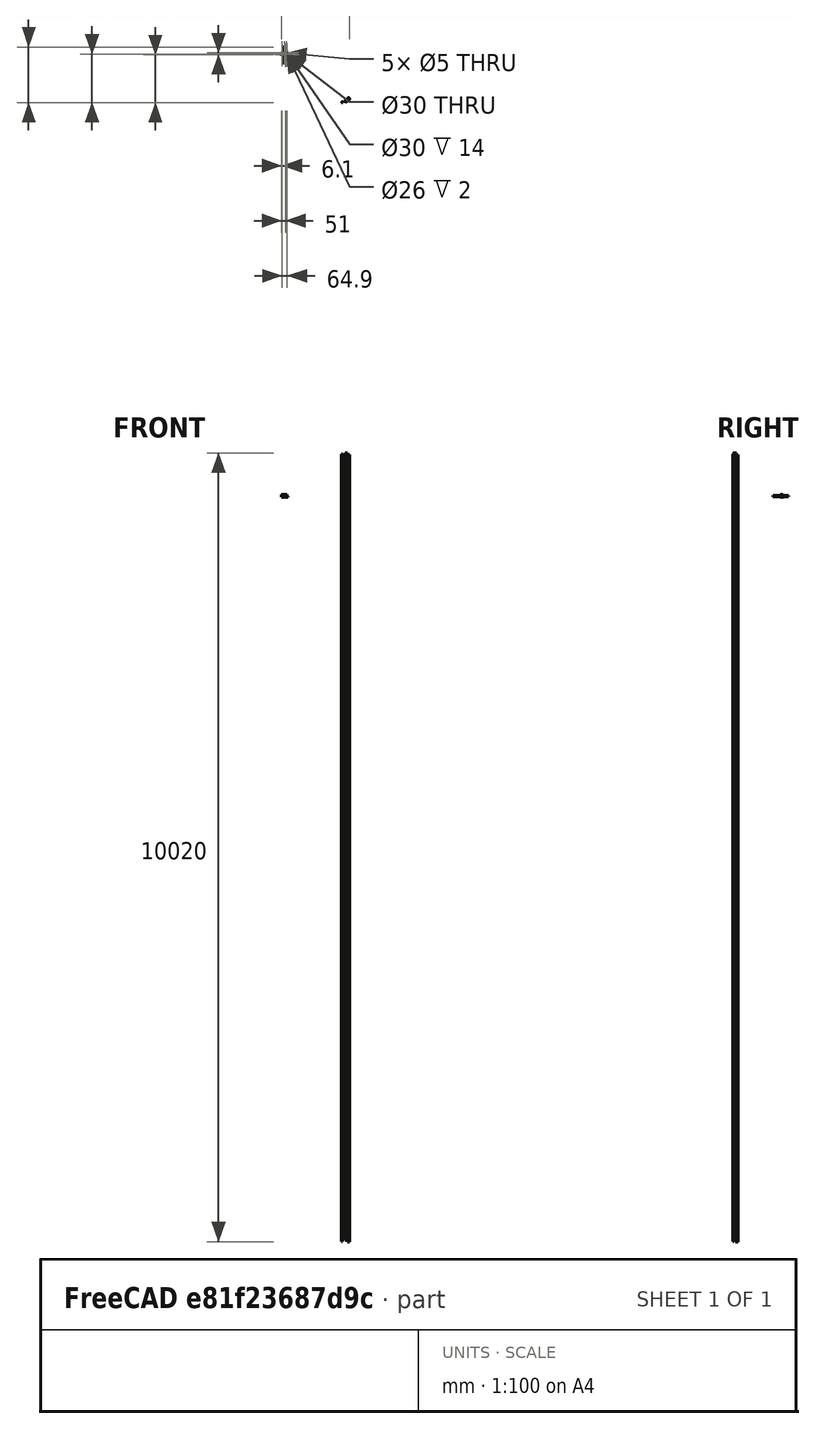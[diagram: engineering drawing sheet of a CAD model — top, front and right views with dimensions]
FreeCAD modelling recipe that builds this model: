
FCSTD DOCUMENT  (FreeCAD 0.15R4671 (Git))
Label: slide_rail_flange_mount_inset
License: CC-BY 3.0
LicenseURL: http://creativecommons.org/licenses/by/3.0/
objects: Sketcher::SketchObject×7, PartDesign::Pocket×6, Part::Cylinder×3, Part::Box×3, Mesh::Feature×2, PartDesign::Fillet×2, PartDesign::Pad×1, Part::Feature×1, Part::MultiFuse×1, Part::Cut×1
note: 32 computed .brp shape members not serialized (recipe doc carries the construction recipe); baked Part::Feature solids carry a one-line shape summary decoded from their .brp

FEATURE [Mesh::Feature] tmp  label="plate"
FEATURE [Part::Cylinder] Cylinder  label="bearing"
  Angle = 360
  Height = 9
  Placement = pos=(-717,613,-534) rot=(0,0,1;0rad)
  Radius = 15
FEATURE [Mesh::Feature] lead_screw_flange  label="lead-screw-flange"
  Placement = pos=(-747,556,-523) rot=(0,0.707107,0.707107;3.14159rad)
FEATURE [Part::Cylinder] Cylinder001  label="lead_screw"
  Angle = 360
  Height = 200
  Placement = pos=(-747,700,-523) rot=(1,0,0;1.5708rad)
  Radius = 5.556
FEATURE [Sketcher::SketchObject] Sketch
  Placement = pos=(-717,613,-525) rot=(0,0,1;0rad)
  Support = -> Cylinder [Face2]
  sketch-geometry (1):
    g0: Circle CenterX=0 CenterY=0 CenterZ=0 NormalX=0 NormalY=0 NormalZ=1 Radius=5
  constraints (2):
    c: Radius(g0) = 5
    c: Coincident(g0,g-1)
FEATURE [PartDesign::Pocket] Pocket
  Length = 5
  Placement = pos=(-717,613,-534) rot=(0,0,1;0rad)
  Sketch = -> Sketch
  Type = 1
FEATURE [Part::Box] Box  label="Cube"
  Height = 4
  Length = 80
  Placement = pos=(-768,594,-534) rot=(0,0,1;0rad)
  Width = 42
FEATURE [Sketcher::SketchObject] Sketch001
  Placement = pos=(-768,594,-530) rot=(0,0,1;0rad)
  Support = -> Box [Face6]
  sketch-geometry (1):
    g0: Circle CenterX=82 CenterY=41 CenterZ=0 NormalX=0 NormalY=0 NormalZ=1 Radius=15
  constraints (3):
    c: DistanceX(g-1,g0) = 82
    c: DistanceY(g-1,g0) = 41
    c: Radius(g0) = 15
FEATURE [PartDesign::Pocket] Pocket001
  Length = 5
  Placement = pos=(-768,594,-534) rot=(0,0,1;0rad)
  Sketch = -> Sketch001
  Type = 1
FEATURE [Part::Box] Box001  label="Cube001"
  Height = 25
  Length = 40
  Placement = pos=(-768,594,-530) rot=(0,0,1;0rad)
  Width = 4
FEATURE [Sketcher::SketchObject] Sketch002
  Placement = pos=(-768,598,-530) rot=(0,0.707107,0.707107;3.14159rad)
  Support = -> Box001 [Face4]
  sketch-geometry (6):
    g0: Circle CenterX=-33.247 CenterY=14 CenterZ=0 NormalX=0 NormalY=0 NormalZ=1 Radius=2.5781
    g1: Circle CenterX=-8.5 CenterY=14 CenterZ=0 NormalX=0 NormalY=0 NormalZ=1 Radius=2.5781
    g2: ArcOfCircle CenterX=-20.85 CenterY=12 CenterZ=0 NormalX=0 NormalY=0 NormalZ=1 Radius=7.15 StartAngle=0 EndAngle=3.14159
    g3: LineSegment StartX=-13.7 StartY=12 StartZ=0 EndX=-13.7 EndY=0 EndZ=0
    g4: LineSegment StartX=-28 StartY=12 StartZ=0 EndX=-28 EndY=0 EndZ=0
    g5: LineSegment StartX=-28 StartY=0 StartZ=0 EndX=-13.7 EndY=0 EndZ=0
  constraints (21):
    c: Radius(g0) = 2.5781
    c: Equal(g0,g1)
    c: DistanceY(g-1,g0) = 14
    c: DistanceY(g-1,g1) = 14
    c: DistanceX(g0,g1) = 24.747
    c: DistanceX(g-1,g1) = -8.5
    c: DistanceY(g-1,g2) = 12
    c: DistanceX(g-1,g2) = -20.85
    c: DistanceY(g-1,g2) = 12
    c: DistanceY(g-1,g2) = 12
    c: DistanceX(g-1,g2) = -28
    c: PointOnObject(g3,g-1)
    c: Vertical(g3)
    c: Tangent(g3,g2)
    c: PointOnObject(g4,g-1)
    c: Vertical(g4)
    c: Tangent(g4,g2)
    c: Coincident(g2,g4)
    c: Coincident(g3,g2)
    c: Coincident(g5,g4)
    c: Coincident(g5,g3)
FEATURE [PartDesign::Pocket] Pocket002
  Length = 5
  Placement = pos=(-768,594,-530) rot=(0,0,1;0rad)
  Sketch = -> Sketch002
  Type = 1
FEATURE [PartDesign::Fillet] Fillet
  Base = -> Pocket002 [Edge15]
  Placement = pos=(-768,594,-530) rot=(0,0,1;0rad)
  Radius = 10
FEATURE [PartDesign::Fillet] Fillet001
  Base = -> Fillet [Edge20]
  Placement = pos=(-768,594,-530) rot=(0,0,1;0rad)
  Radius = 10
FEATURE [Sketcher::SketchObject] Sketch003
  Placement = pos=(-768,594,-530) rot=(0,0,1;0rad)
  Support = -> Pocket001 [Face3]
  sketch-geometry (1):
    g0: Circle CenterX=51 CenterY=19 CenterZ=0 NormalX=0 NormalY=0 NormalZ=1 Radius=17
  constraints (3):
    c: Radius(g0) = 17
    c: DistanceY(g-1,g0) = 19
    c: DistanceX(g-1,g0) = 51
FEATURE [PartDesign::Pad] Pad
  Length = 20
  Length2 = 100
  Placement = pos=(-768,594,-534) rot=(0,0,1;0rad)
  Sketch = -> Sketch003
  Type = 0
FEATURE [Sketcher::SketchObject] Sketch004
  Placement = pos=(-768,594,-510) rot=(0,0,1;0rad)
  Support = -> Pad [Face9]
  sketch-geometry (1):
    g0: Circle CenterX=51 CenterY=19 CenterZ=0 NormalX=0 NormalY=0 NormalZ=1 Radius=15
  constraints (3):
    c: Radius(g0) = 15
    c: DistanceX(g-1,g0) = 51
    c: DistanceY(g-1,g0) = 19
FEATURE [PartDesign::Pocket] Pocket003
  Length = 30
  Placement = pos=(-768,594,-534) rot=(0,0,1;0rad)
  Sketch = -> Sketch004
  Type = 1
FEATURE [Sketcher::SketchObject] Sketch005
  Placement = pos=(-768,594,-530) rot=(0,0,1;0rad)
  Support = -> Pocket003 [Face3]
  sketch-geometry (5):
    g0: Circle CenterX=6.1 CenterY=34 CenterZ=0 NormalX=0 NormalY=0 NormalZ=1 Radius=2.5
    g1: Circle CenterX=6.1 CenterY=14 CenterZ=0 NormalX=0 NormalY=0 NormalZ=1 Radius=2.5
    g2: Circle CenterX=35.9 CenterY=34 CenterZ=0 NormalX=0 NormalY=0 NormalZ=1 Radius=2.5
    g3: Circle CenterX=64 CenterY=36 CenterZ=0 NormalX=0 NormalY=0 NormalZ=1 Radius=2.5
    g4: Circle CenterX=71 CenterY=10 CenterZ=0 NormalX=0 NormalY=0 NormalZ=1 Radius=2.5
  constraints (15):
    c: Radius(g0) = 2.5
    c: Equal(g0,g1)
    c: Equal(g1,g2)
    c: Equal(g2,g3)
    c: Equal(g3,g4)
    c: DistanceY(g-1,g1) = 14
    c: DistanceY(g1,g0) = 20
    c: DistanceY(g-1,g4) = 10
    c: DistanceY(g3,g4) = -26
    c: DistanceY(g-1,g2) = 34
    c: DistanceX(g-1,g0) = 6.1
    c: DistanceX(g-1,g1) = 6.1
    c: DistanceX(g-1,g2) = 35.9
    c: DistanceX(g-1,g4) = 71
    c: DistanceX(g-1,g3) = 64
FEATURE [PartDesign::Pocket] Pocket004
  Length = 5
  Placement = pos=(-768,594,-534) rot=(0,0,1;0rad)
  Sketch = -> Sketch005
  Type = 1
FEATURE [Part::Feature] Chamfer001001  label="Chamfer002"
  shape: bbox 80 x 42 x 29 mm, 27 faces (baked)
FEATURE [Part::Box] Box002  label="Cube002"
  Height = 10
  Length = 12
  Placement = pos=(-753,591,-536) rot=(0,0,1;0rad)
  Width = 50
FEATURE [Part::Cylinder] Cylinder002  label="Cylinder"
  Angle = 360
  Height = 2
  Placement = pos=(-717,613,-510) rot=(0,0,1;0rad)
  Radius = 17
FEATURE [Sketcher::SketchObject] Sketch006
  Placement = pos=(-717,613,-508) rot=(0,0,1;0rad)
  Support = -> Cylinder002 [Face2]
  sketch-geometry (1):
    g0: Circle CenterX=0 CenterY=0 CenterZ=0 NormalX=0 NormalY=0 NormalZ=1 Radius=13
  constraints (2):
    c: Coincident(g0,g-1)
    c: Radius(g0) = 13
FEATURE [PartDesign::Pocket] Pocket005
  Length = 5
  Placement = pos=(-717,613,-510) rot=(0,0,1;0rad)
  Sketch = -> Sketch006
  Type = 0
FEATURE [Part::MultiFuse] Fusion
  Shapes = -> [Chamfer001001,Pocket005,Fillet001,Pocket004]
FEATURE [Part::Cut] Cut
  Base = -> Fusion
  Tool = -> Box002
